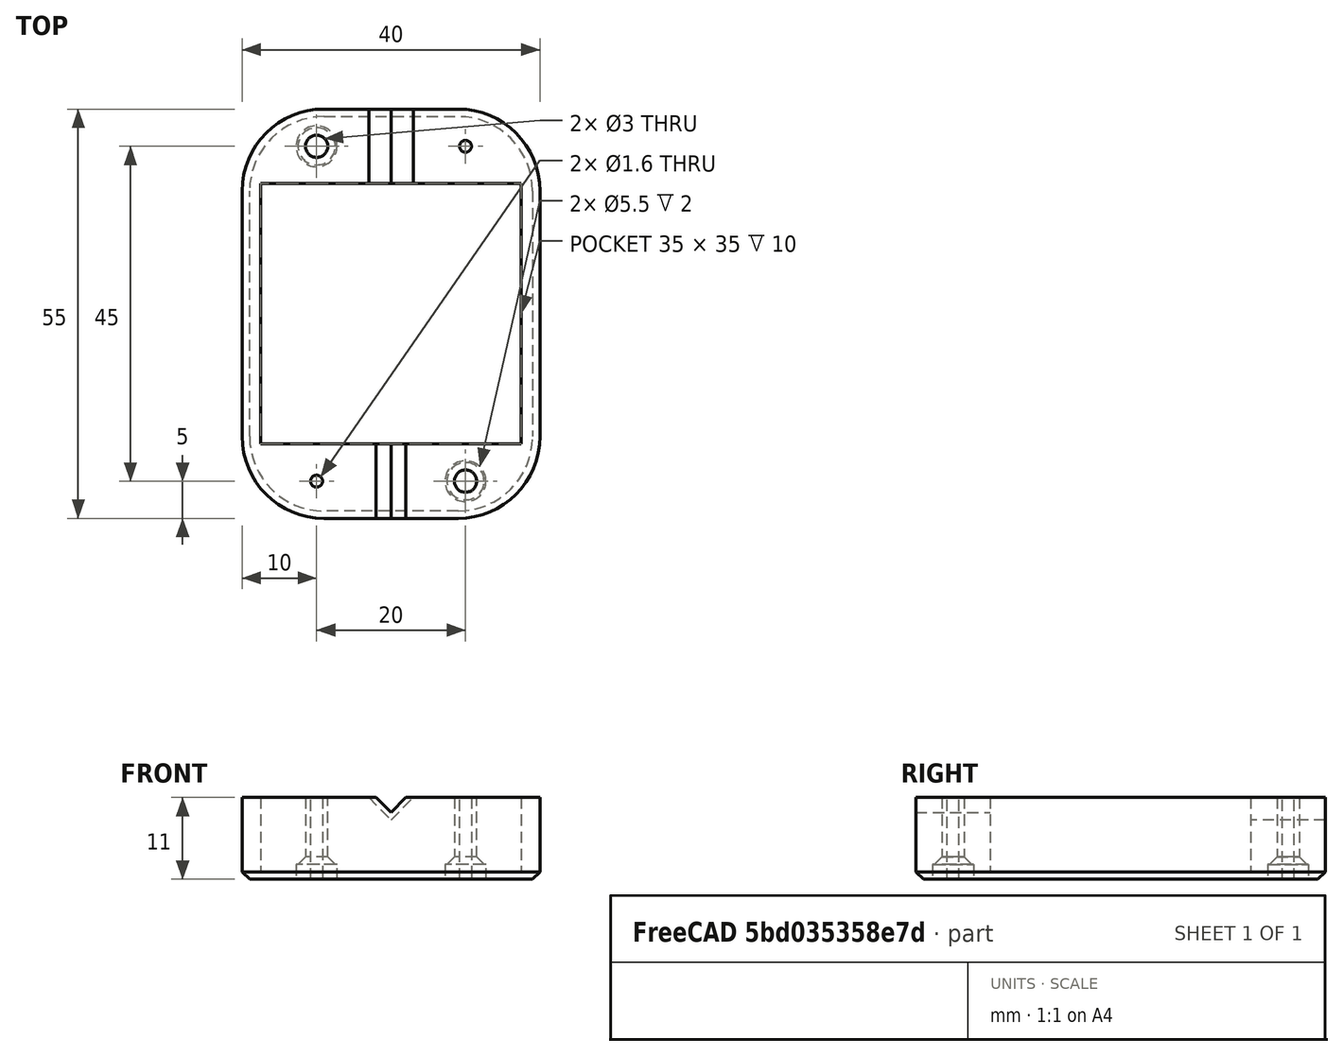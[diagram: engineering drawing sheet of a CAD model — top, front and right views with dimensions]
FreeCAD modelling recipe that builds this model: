
FCSTD DOCUMENT  (FreeCAD 0.19R)
Label: SparkBuckBoostHole
License: All rights reserved
LicenseURL: http://en.wikipedia.org/wiki/All_rights_reserved
objects: Sketcher::SketchObject×7, PartDesign::Pocket×6, PartDesign::Chamfer×2, PartDesign::Pad×1, PartDesign::Fillet×1, PartDesign::Body×1, Mesh::Feature×1
note: 28 computed .brp shape members not serialized (recipe doc carries the construction recipe); baked Part::Feature solids carry a one-line shape summary decoded from their .brp

FEATURE [Sketcher::SketchObject] Sketch
  FullyConstrained = true
  MapMode = 5
  Support = -> [XY_Plane]
  sketch-geometry (4):
    g0: LineSegment StartX=-20 StartY=27.5 StartZ=0 EndX=20 EndY=27.5 EndZ=0
    g1: LineSegment StartX=20 StartY=27.5 StartZ=0 EndX=20 EndY=-27.5 EndZ=0
    g2: LineSegment StartX=20 StartY=-27.5 StartZ=0 EndX=-20 EndY=-27.5 EndZ=0
    g3: LineSegment StartX=-20 StartY=-27.5 StartZ=0 EndX=-20 EndY=27.5 EndZ=0
  constraints (11):
    c: Coincident(g0,g1)
    c: Coincident(g1,g2)
    c: Coincident(g2,g3)
    c: Coincident(g3,g0)
    c: Horizontal(g0)
    c: Horizontal(g2)
    c: Vertical(g1)
    c: Vertical(g3)
    c: Symmetric(g1,g0,g-1)
    c: Distance(g0) = 40
    c: Distance(g1) = 55
FEATURE [PartDesign::Pad] Pad
  Direction = (1,1,1)
  Length = 11
  Length2 = 100
  Profile = -> Sketch
  Type = 0
FEATURE [Sketcher::SketchObject] Sketch001
  FullyConstrained = true
  MapMode = 5
  Placement = pos=(0,0,11) rot=(0,0,1;0rad)
  Support = -> [Pad]
  sketch-geometry (4):
    g0: LineSegment StartX=-17.5 StartY=17.5 StartZ=0 EndX=17.5 EndY=17.5 EndZ=0
    g1: LineSegment StartX=17.5 StartY=17.5 StartZ=0 EndX=17.5 EndY=-17.5 EndZ=0
    g2: LineSegment StartX=17.5 StartY=-17.5 StartZ=0 EndX=-17.5 EndY=-17.5 EndZ=0
    g3: LineSegment StartX=-17.5 StartY=-17.5 StartZ=0 EndX=-17.5 EndY=17.5 EndZ=0
  constraints (11):
    c: Coincident(g0,g1)
    c: Coincident(g1,g2)
    c: Coincident(g2,g3)
    c: Coincident(g3,g0)
    c: Horizontal(g0)
    c: Horizontal(g2)
    c: Vertical(g1)
    c: Vertical(g3)
    c: Symmetric(g1,g0,g-1)
    c: Distance(g0) = 35
    c: Equal(g2,g3)
FEATURE [PartDesign::Pocket] Pocket
  BaseFeature = -> Pad
  Length = 10
  Length2 = 100
  Profile = -> Sketch001
  Type = 0
FEATURE [Sketcher::SketchObject] Sketch002
  ExternalGeometry = -> [Pocket]
  FullyConstrained = true
  MapMode = 5
  Placement = pos=(0,27.5,0) rot=(0,0.707107,0.707107;3.14159rad)
  Support = -> [Pocket]
  sketch-geometry (3):
    g0: LineSegment StartX=14.425 StartY=22.425 StartZ=0 EndX=0 EndY=8 EndZ=0
    g1: LineSegment StartX=0 StartY=8 StartZ=0 EndX=-14.425 EndY=22.425 EndZ=0
    g2: LineSegment StartX=-14.425 StartY=22.425 StartZ=0 EndX=14.425 EndY=22.425 EndZ=0
  constraints (9):
    c: PointOnObject(g0,g-2)
    c: Coincident(g0,g1)
    c: Coincident(g1,g2)
    c: Coincident(g2,g0)
    c: Perpendicular(g1,g0)
    c: Angle(g0) = -2.35619
    c: Horizontal(g2)
    c: Distance(g0) = 20.4
    c: Distance(g0,g-3) = 3
FEATURE [PartDesign::Pocket] Pocket001
  BaseFeature = -> Pocket
  Length = 16
  Length2 = 100
  Profile = -> Sketch002
  Type = 0
FEATURE [Sketcher::SketchObject] Sketch003
  ExternalGeometry = -> [Pocket001]
  FullyConstrained = true
  MapMode = 5
  Placement = pos=(0,-27.5,0) rot=(1,0,0;1.5708rad)
  Support = -> [Pocket001]
  sketch-geometry (3):
    g0: LineSegment StartX=10 StartY=19 StartZ=0 EndX=0 EndY=9 EndZ=0
    g1: LineSegment StartX=0 StartY=9 StartZ=0 EndX=-10 EndY=19 EndZ=0
    g2: LineSegment StartX=-10 StartY=19 StartZ=0 EndX=10 EndY=19 EndZ=0
  constraints (8):
    c: PointOnObject(g0,g-2)
    c: Coincident(g0,g1)
    c: Coincident(g1,g2)
    c: Coincident(g2,g0)
    c: Symmetric(g0,g1,g-2)
    c: Distance(g2) = 20
    c: Perpendicular(g1,g0)
    c: Distance(g0,g-3) = 2
FEATURE [PartDesign::Pocket] Pocket002
  BaseFeature = -> Pocket001
  Length = 16
  Length2 = 100
  Profile = -> Sketch003
  Type = 0
FEATURE [Sketcher::SketchObject] Sketch004
  ExternalGeometry = -> [Pocket002]
  FullyConstrained = true
  MapMode = 5
  Placement = pos=(0,0,11) rot=(0,0,1;0rad)
  Support = -> [Pocket002]
  sketch-geometry (4):
    g0: Circle CenterX=-10 CenterY=22.5 CenterZ=0 NormalX=0 NormalY=0 NormalZ=1 AngleXU=0 Radius=0.8
    g1: Circle CenterX=10 CenterY=22.5 CenterZ=0 NormalX=0 NormalY=0 NormalZ=1 AngleXU=0 Radius=0.8
    g2: Circle CenterX=-10 CenterY=-22.5 CenterZ=0 NormalX=0 NormalY=0 NormalZ=1 AngleXU=0 Radius=0.8
    g3: Circle CenterX=10 CenterY=-22.5 CenterZ=0 NormalX=0 NormalY=0 NormalZ=1 AngleXU=0 Radius=0.8
  constraints (10):
    c: Radius(g3) = 0.8
    c: Equal(g3,g2)
    c: Equal(g3,g0)
    c: Equal(g3,g1)
    c: Symmetric(g1,g0,g-2)
    c: Symmetric(g3,g2,g-2)
    c: Distance(g1,g-4) = 5
    c: Distance(g3,g-3) = 5
    c: Distance(g3,g2) = 20
    c: Distance(g1,g0) = 20
FEATURE [PartDesign::Pocket] Pocket003
  BaseFeature = -> Pocket002
  Length = 5
  Length2 = 100
  Profile = -> Sketch004
  Type = 1
FEATURE [Sketcher::SketchObject] Sketch005
  ExternalGeometry = -> [Pocket003]
  FullyConstrained = true
  MapMode = 5
  Placement = pos=(0,0,0) rot=(1,0,0;3.14159rad)
  Support = -> [Pocket003]
  sketch-geometry (2):
    g0: Circle CenterX=10 CenterY=22.5 CenterZ=0 NormalX=0 NormalY=0 NormalZ=1 AngleXU=0 Radius=1.5
    g1: Circle CenterX=-10 CenterY=-22.5 CenterZ=0 NormalX=0 NormalY=0 NormalZ=1 AngleXU=0 Radius=1.5
  constraints (4):
    c: Radius(g1) = 1.5
    c: Equal(g1,g0)
    c: Coincident(g0,g-3)
    c: Coincident(g1,g-5)
FEATURE [PartDesign::Pocket] Pocket004
  BaseFeature = -> Pocket003
  Length = 5
  Length2 = 100
  Profile = -> Sketch005
  Type = 1
FEATURE [Sketcher::SketchObject] Sketch006
  ExternalGeometry = -> [Pocket004]
  FullyConstrained = true
  MapMode = 5
  Placement = pos=(0,0,0) rot=(1,0,0;3.14159rad)
  Support = -> [Pocket004]
  sketch-geometry (2):
    g0: Circle CenterX=10 CenterY=22.5 CenterZ=0 NormalX=0 NormalY=0 NormalZ=1 AngleXU=0 Radius=2.75
    g1: Circle CenterX=-10 CenterY=-22.5 CenterZ=0 NormalX=0 NormalY=0 NormalZ=1 AngleXU=0 Radius=2.75
  constraints (4):
    c: Radius(g1) = 2.75
    c: Equal(g1,g0)
    c: Coincident(g0,g-4)
    c: Coincident(g1,g-3)
FEATURE [PartDesign::Pocket] Pocket005
  BaseFeature = -> Pocket004
  Length = 2
  Length2 = 100
  Profile = -> Sketch006
  Type = 0
FEATURE [PartDesign::Fillet] Fillet
  Base = -> Pocket005 [Edge2,Edge15,Edge7,Edge37]
  BaseFeature = -> Pocket005
  Radius = 11
  SupportTransform = false
FEATURE [PartDesign::Chamfer] Chamfer
  Angle = 45
  Base = -> Fillet [Edge11]
  BaseFeature = -> Fillet
  ChamferType = 0
  FlipDirection = false
  Size = 1
  Size2 = 1
  SupportTransform = false
FEATURE [PartDesign::Chamfer] Chamfer001
  Angle = 45
  Base = -> Chamfer [Edge72,Edge78]
  BaseFeature = -> Chamfer
  ChamferType = 0
  FlipDirection = false
  Size = 1
  Size2 = 1
  SupportTransform = false
FEATURE [PartDesign::Body] Body
  Group = -> [Sketch,Pad,Sketch001,Pocket,Sketch002,Pocket001,Sketch003,Pocket002,Sketch004,Pocket003,Sketch005,Pocket004,Sketch006,Pocket005,Fillet,Chamfer,Chamfer001]
  Origin = -> Origin
  Tip = -> Chamfer001
FEATURE [Mesh::Feature] Mesh  label="Chamfer001 (Meshed)"
